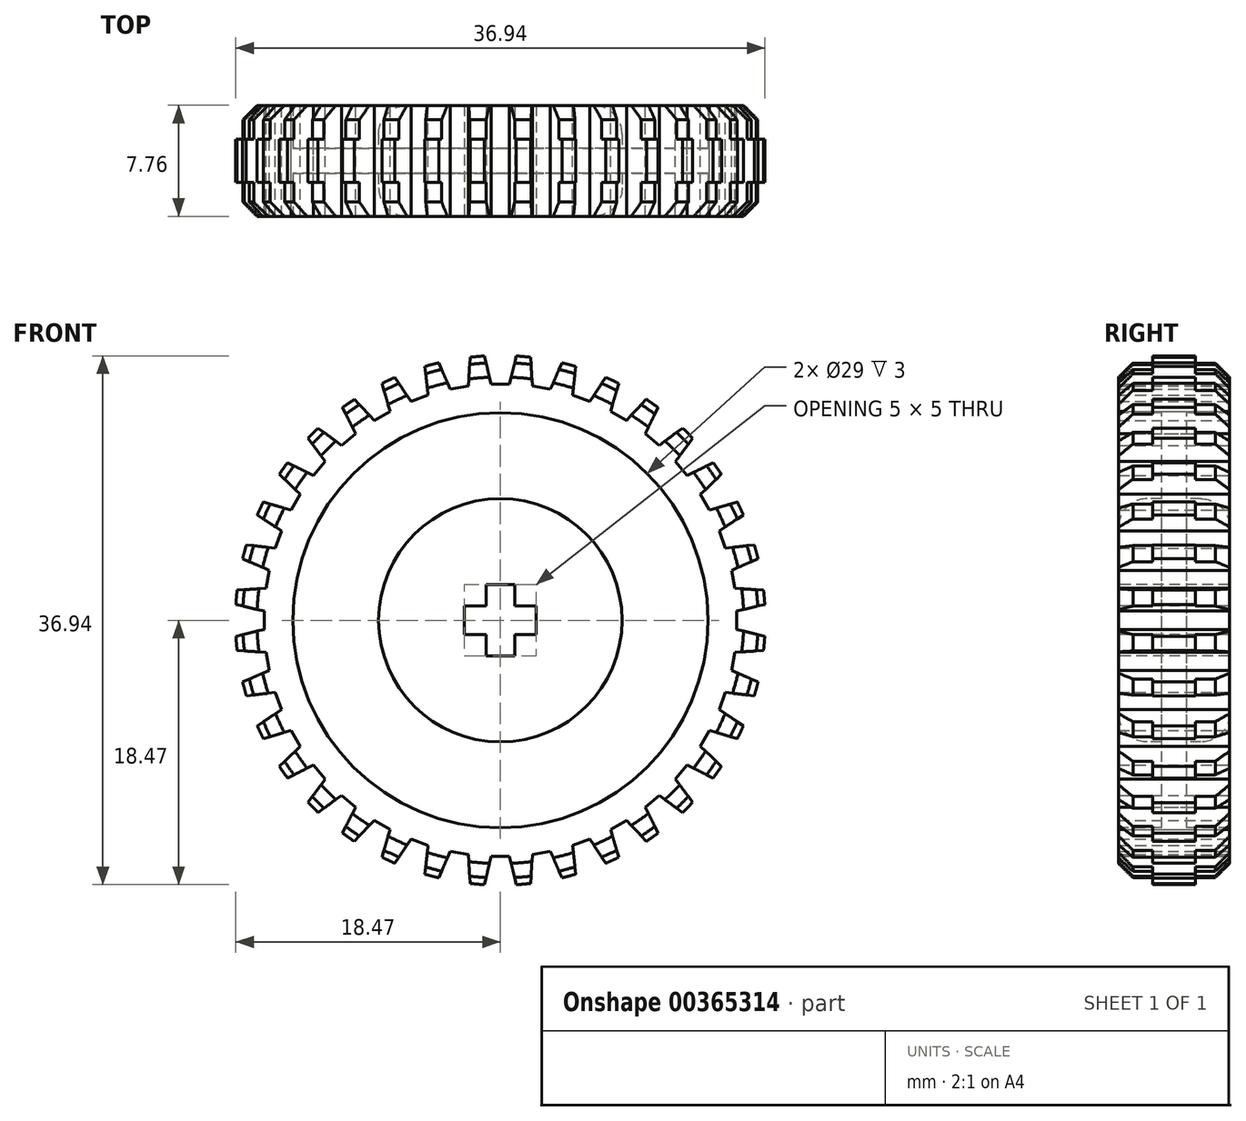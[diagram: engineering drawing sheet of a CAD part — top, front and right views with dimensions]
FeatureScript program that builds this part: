
annotation { "Feature Type Name" : "Feature", "Feature Type Description" : "" }
export const myFeature = defineFeature(function(context is Context, id is Id, definition is map)
    precondition{}
    {
        {
            var Q0;
            Q0=qCreatedBy(makeId("Right.planeOp"),FACE);
            var sketch = newSketch(context, id + "F0", { "sketchPlane" : qUnion([Q0])});
            skLineSegment(sketch, "E0", {"start": v(0, 0) * mm, "end": v(0, 18.5) * mm, "construction": true});
            skLineSegment(sketch, "E1", {"start": v(0, 0) * mm, "end": v(13.72, 0) * mm, "construction": true});
            skLineSegment(sketch, "E2", {"start": v(3.88, 6.5) * mm, "end": v(3.88, 0) * mm});
            skPoint(sketch, "E3.visualSharp", {"position": v(3.88, 18.5) * mm});
            skPoint(sketch, "E4.visualSharp", {"position": v(3.88, 8.5) * mm});
            skArc(sketch, "E4.filletArc", {"start": v(3.88, 6.5) * mm, "mid": v(3.29, 7.91) * mm, "end": v(1.88, 8.5) * mm});
            skArc(sketch, "E5.MirrorCS", {"start": v(-3.88, 6.5) * mm, "mid": v(-3.29, 7.91) * mm, "end": v(-1.88, 8.5) * mm});
            skLineSegment(sketch, "E6.MirrorCS", {"start": v(-3.88, 6.5) * mm, "end": v(-3.88, 0) * mm});
            skLineSegment(sketch, "E7", {"start": v(-3.88, 0) * mm, "end": v(3.88, 0) * mm});
            skLineSegment(sketch, "E8", {"start": v(0, 18.5) * mm, "end": v(1.5, 18.5) * mm});
            skLineSegment(sketch, "E9", {"start": v(3.88, 18) * mm, "end": v(3.88, 14.5) * mm});
            skLineSegment(sketch, "E10", {"start": v(3.88, 14.5) * mm, "end": v(0.87, 14.5) * mm});
            skLineSegment(sketch, "E11", {"start": v(0.87, 14.5) * mm, "end": v(0.87, 8.5) * mm});
            skLineSegment(sketch, "E12", {"start": v(0.87, 8.5) * mm, "end": v(1.88, 8.5) * mm});
            skLineSegment(sketch, "E13.MirrorCS", {"start": v(-3.88, 14.5) * mm, "end": v(-0.87, 14.5) * mm});
            skLineSegment(sketch, "E14.MirrorCS", {"start": v(-0.87, 14.5) * mm, "end": v(-0.87, 8.5) * mm});
            skLineSegment(sketch, "E15.MirrorCS", {"start": v(-0.87, 8.5) * mm, "end": v(-1.88, 8.5) * mm});
            skLineSegment(sketch, "E16", {"start": v(1.5, 18.5) * mm, "end": v(1.5, 18) * mm});
            skLineSegment(sketch, "E17", {"start": v(1.5, 18) * mm, "end": v(3.88, 18) * mm});
            skLineSegment(sketch, "E18", {"start": v(3.88, 18) * mm, "end": v(3.88, 18.5) * mm, "construction": true});
            skLineSegment(sketch, "E19", {"start": v(1.5, 18.5) * mm, "end": v(3.88, 18.5) * mm, "construction": true});
            skLineSegment(sketch, "E20.MirrorCS", {"start": v(0, 18.5) * mm, "end": v(-1.5, 18.5) * mm});
            skLineSegment(sketch, "E21.MirrorCS", {"start": v(-1.5, 18.5) * mm, "end": v(-1.5, 18) * mm});
            skLineSegment(sketch, "E22.MirrorCS", {"start": v(-1.5, 18) * mm, "end": v(-3.88, 18) * mm});
            skLineSegment(sketch, "E23.MirrorCS", {"start": v(-3.88, 18) * mm, "end": v(-3.88, 14.5) * mm});
            skSolve(sketch);
        }
        {
            var Q0;
            Q0=makeQuery(id+"F0.imprint","IMPRINT",FACE,{"disambiguationData":[TD([[makeQuery(id+"F0.imprint","IMPRINT",EDGE,{"derivedFrom":sQuery(id+"F0.wireOp",EDGE,"E2")}),-1.0]])]});
            var Q1;
            Q1=sQuery(id+"F0.wireOp",EDGE,"E1");
            revolve(context, id + "F1", {"entities" : qUnion([Q0]), "axis" : qUnion([Q1]), "revolveType" : RevolveType.FULL});
        }
        {
            var Q0;
            Q0=makeQuery(id+"F1.opRevolve","SWEPT_EDGE",EDGE,{"disambiguationData":[OSD([sQuery(id+"F0.wireOp",EDGE,"E22.MirrorCS"),sQuery(id+"F0.wireOp",EDGE,"E23.MirrorCS")])]});
            var Q1;
            Q1=makeQuery(id+"F1.opRevolve","SWEPT_EDGE",EDGE,{"disambiguationData":[OSD([sQuery(id+"F0.wireOp",EDGE,"E9"),sQuery(id+"F0.wireOp",EDGE,"E17")])]});
            chamfer(context, id + "F2", {"entities" : qUnion([Q0, Q1]), "chamferType" : ChamferType.TWO_OFFSETS, "width1" : 1 * mm, "oppositeDirection" : false, "width2" : 1 * mm, "tangentPropagation" : true});
        }
        {
            var Q0;
            Q0=makeQuery(id+"F1.opRevolve","SWEPT_FACE",FACE,{"disambiguationData":[OSD([sQuery(id+"F0.wireOp",EDGE,"E9")])]});
            var sketch = newSketch(context, id + "F3", { "sketchPlane" : qUnion([Q0])});
            skLineSegment(sketch, "E24", {"start": v(0, -14.33) * mm, "end": v(0, 10.6) * mm, "construction": true});
            skLineSegment(sketch, "E25", {"start": v(-15.88, 1.94) * mm, "end": v(5.64, 1.94) * mm, "construction": true});
            skLineSegment(sketch, "E26", {"start": v(0, 0) * mm, "end": v(-1.61, 18.43) * mm, "construction": true});
            skLineSegment(sketch, "E27", {"start": v(-0.9, 15.97) * mm, "end": v(-0.9, 15.97) * mm});
            skArc(sketch, "E28", {"start": v(-0.9, 15.97) * mm, "mid": v(0, -16) * mm, "end": v(0.9, 15.97) * mm, "construction": true});
            skLineSegment(sketch, "E29", {"start": v(0, 10.6) * mm, "end": v(0, 19.08) * mm, "construction": true});
            skLineSegment(sketch, "E30", {"start": v(0, 16) * mm, "end": v(0, 16.5) * mm});
            skLineSegment(sketch, "E31", {"start": v(0, 16.5) * mm, "end": v(-0.64, 16.5) * mm});
            skLineSegment(sketch, "E32", {"start": v(-0.64, 16.5) * mm, "end": v(-1.44, 16.43) * mm});
            skLineSegment(sketch, "E33", {"start": v(-1.11, 18.47) * mm, "end": v(-0.64, 16.5) * mm});
            skLineSegment(sketch, "E34.MirrorCS", {"start": v(0, 16.5) * mm, "end": v(0.64, 16.5) * mm});
            skLineSegment(sketch, "E35.MirrorCS", {"start": v(1.11, 18.47) * mm, "end": v(0.64, 16.5) * mm});
            skLineSegment(sketch, "E36", {"start": v(-1.61, 18.43) * mm, "end": v(-1.11, 18.47) * mm});
            skLineSegment(sketch, "E37.MirrorCS", {"start": v(1.61, 18.43) * mm, "end": v(1.11, 18.47) * mm});
            skLineSegment(sketch, "E38.1.0", {"start": v(-4.79, 17.87) * mm, "end": v(-4.3, 18) * mm});
            skLineSegment(sketch, "E38.1.1", {"start": v(-4.3, 18) * mm, "end": v(-3.5, 16.14) * mm});
            skLineSegment(sketch, "E38.1.2", {"start": v(-2.87, 16.25) * mm, "end": v(-3.5, 16.14) * mm});
            skLineSegment(sketch, "E38.1.3", {"start": v(-2.87, 16.25) * mm, "end": v(-2.23, 16.36) * mm});
            skLineSegment(sketch, "E38.1.4", {"start": v(-2.11, 18.39) * mm, "end": v(-2.23, 16.36) * mm});
            skLineSegment(sketch, "E38.1.5", {"start": v(-1.61, 18.43) * mm, "end": v(-2.11, 18.39) * mm});
            skLineSegment(sketch, "E38.2.0", {"start": v(-7.82, 16.77) * mm, "end": v(-7.37, 16.98) * mm});
            skLineSegment(sketch, "E38.2.1", {"start": v(-7.37, 16.98) * mm, "end": v(-6.25, 15.29) * mm});
            skLineSegment(sketch, "E38.2.2", {"start": v(-5.64, 15.5) * mm, "end": v(-6.25, 15.29) * mm});
            skLineSegment(sketch, "E38.2.3", {"start": v(-5.64, 15.5) * mm, "end": v(-5.04, 15.72) * mm});
            skLineSegment(sketch, "E38.2.4", {"start": v(-5.27, 17.74) * mm, "end": v(-5.04, 15.72) * mm});
            skLineSegment(sketch, "E38.2.5", {"start": v(-4.79, 17.87) * mm, "end": v(-5.27, 17.74) * mm});
            skLineSegment(sketch, "E39.1.3.0", {"start": v(-10.61, 15.15) * mm, "end": v(-10.2, 15.44) * mm});
            skLineSegment(sketch, "E39.3.3.0", {"start": v(-10.2, 15.44) * mm, "end": v(-8.8, 13.97) * mm});
            skLineSegment(sketch, "E39.6.3.0", {"start": v(-8.25, 14.29) * mm, "end": v(-8.8, 13.97) * mm});
            skLineSegment(sketch, "E39.9.3.0", {"start": v(-8.25, 14.29) * mm, "end": v(-7.7, 14.6) * mm});
            skLineSegment(sketch, "E39.12.3.0", {"start": v(-8.27, 16.56) * mm, "end": v(-7.7, 14.6) * mm});
            skLineSegment(sketch, "E39.15.3.0", {"start": v(-7.82, 16.77) * mm, "end": v(-8.27, 16.56) * mm});
            skLineSegment(sketch, "E39.1.4.0", {"start": v(-13.08, 13.08) * mm, "end": v(-12.73, 13.44) * mm});
            skLineSegment(sketch, "E39.3.4.0", {"start": v(-12.73, 13.44) * mm, "end": v(-11.1, 12.23) * mm});
            skLineSegment(sketch, "E39.6.4.0", {"start": v(-10.6, 12.64) * mm, "end": v(-11.1, 12.23) * mm});
            skLineSegment(sketch, "E39.9.4.0", {"start": v(-10.6, 12.64) * mm, "end": v(-10.12, 13.05) * mm});
            skLineSegment(sketch, "E39.12.4.0", {"start": v(-11.02, 14.87) * mm, "end": v(-10.12, 13.05) * mm});
            skLineSegment(sketch, "E39.15.4.0", {"start": v(-10.61, 15.15) * mm, "end": v(-11.02, 14.87) * mm});
            skLineSegment(sketch, "E39.1.5.0", {"start": v(-15.15, 10.61) * mm, "end": v(-14.87, 11.02) * mm});
            skLineSegment(sketch, "E39.3.5.0", {"start": v(-14.87, 11.02) * mm, "end": v(-13.05, 10.12) * mm});
            skLineSegment(sketch, "E39.6.5.0", {"start": v(-12.64, 10.6) * mm, "end": v(-13.05, 10.12) * mm});
            skLineSegment(sketch, "E39.9.5.0", {"start": v(-12.64, 10.6) * mm, "end": v(-12.23, 11.1) * mm});
            skLineSegment(sketch, "E39.12.5.0", {"start": v(-13.44, 12.73) * mm, "end": v(-12.23, 11.1) * mm});
            skLineSegment(sketch, "E39.15.5.0", {"start": v(-13.08, 13.08) * mm, "end": v(-13.44, 12.73) * mm});
            skLineSegment(sketch, "E39.1.6.0", {"start": v(-16.77, 7.82) * mm, "end": v(-16.56, 8.27) * mm});
            skLineSegment(sketch, "E39.3.6.0", {"start": v(-16.56, 8.27) * mm, "end": v(-14.6, 7.7) * mm});
            skLineSegment(sketch, "E39.6.6.0", {"start": v(-14.29, 8.25) * mm, "end": v(-14.6, 7.7) * mm});
            skLineSegment(sketch, "E39.9.6.0", {"start": v(-14.29, 8.25) * mm, "end": v(-13.97, 8.8) * mm});
            skLineSegment(sketch, "E39.12.6.0", {"start": v(-15.44, 10.2) * mm, "end": v(-13.97, 8.8) * mm});
            skLineSegment(sketch, "E39.15.6.0", {"start": v(-15.15, 10.61) * mm, "end": v(-15.44, 10.2) * mm});
            skLineSegment(sketch, "E39.1.7.0", {"start": v(-17.87, 4.79) * mm, "end": v(-17.74, 5.27) * mm});
            skLineSegment(sketch, "E39.3.7.0", {"start": v(-17.74, 5.27) * mm, "end": v(-15.72, 5.04) * mm});
            skLineSegment(sketch, "E39.6.7.0", {"start": v(-15.5, 5.64) * mm, "end": v(-15.72, 5.04) * mm});
            skLineSegment(sketch, "E39.9.7.0", {"start": v(-15.5, 5.64) * mm, "end": v(-15.29, 6.25) * mm});
            skLineSegment(sketch, "E39.12.7.0", {"start": v(-16.98, 7.37) * mm, "end": v(-15.29, 6.25) * mm});
            skLineSegment(sketch, "E39.15.7.0", {"start": v(-16.77, 7.82) * mm, "end": v(-16.98, 7.37) * mm});
            skLineSegment(sketch, "E39.1.8.0", {"start": v(-18.43, 1.61) * mm, "end": v(-18.39, 2.11) * mm});
            skLineSegment(sketch, "E39.3.8.0", {"start": v(-18.39, 2.11) * mm, "end": v(-16.36, 2.23) * mm});
            skLineSegment(sketch, "E39.6.8.0", {"start": v(-16.25, 2.87) * mm, "end": v(-16.36, 2.23) * mm});
            skLineSegment(sketch, "E39.9.8.0", {"start": v(-16.25, 2.87) * mm, "end": v(-16.14, 3.5) * mm});
            skLineSegment(sketch, "E39.12.8.0", {"start": v(-18, 4.3) * mm, "end": v(-16.14, 3.5) * mm});
            skLineSegment(sketch, "E39.15.8.0", {"start": v(-17.87, 4.79) * mm, "end": v(-18, 4.3) * mm});
            skLineSegment(sketch, "E39.1.9.0", {"start": v(-18.43, -1.61) * mm, "end": v(-18.47, -1.11) * mm});
            skLineSegment(sketch, "E39.3.9.0", {"start": v(-18.47, -1.11) * mm, "end": v(-16.5, -0.64) * mm});
            skLineSegment(sketch, "E39.6.9.0", {"start": v(-16.5, 0) * mm, "end": v(-16.5, -0.64) * mm});
            skLineSegment(sketch, "E39.9.9.0", {"start": v(-16.5, 0) * mm, "end": v(-16.5, 0.64) * mm});
            skLineSegment(sketch, "E39.12.9.0", {"start": v(-18.47, 1.11) * mm, "end": v(-16.5, 0.64) * mm});
            skLineSegment(sketch, "E39.15.9.0", {"start": v(-18.43, 1.61) * mm, "end": v(-18.47, 1.11) * mm});
            skLineSegment(sketch, "E39.1.10.0", {"start": v(-17.87, -4.79) * mm, "end": v(-18, -4.3) * mm});
            skLineSegment(sketch, "E39.3.10.0", {"start": v(-18, -4.3) * mm, "end": v(-16.14, -3.5) * mm});
            skLineSegment(sketch, "E39.6.10.0", {"start": v(-16.25, -2.87) * mm, "end": v(-16.14, -3.5) * mm});
            skLineSegment(sketch, "E39.9.10.0", {"start": v(-16.25, -2.87) * mm, "end": v(-16.36, -2.23) * mm});
            skLineSegment(sketch, "E39.12.10.0", {"start": v(-18.39, -2.11) * mm, "end": v(-16.36, -2.23) * mm});
            skLineSegment(sketch, "E39.15.10.0", {"start": v(-18.43, -1.61) * mm, "end": v(-18.39, -2.11) * mm});
            skLineSegment(sketch, "E39.1.11.0", {"start": v(-16.77, -7.82) * mm, "end": v(-16.98, -7.37) * mm});
            skLineSegment(sketch, "E39.3.11.0", {"start": v(-16.98, -7.37) * mm, "end": v(-15.29, -6.25) * mm});
            skLineSegment(sketch, "E39.6.11.0", {"start": v(-15.5, -5.64) * mm, "end": v(-15.29, -6.25) * mm});
            skLineSegment(sketch, "E39.9.11.0", {"start": v(-15.5, -5.64) * mm, "end": v(-15.72, -5.04) * mm});
            skLineSegment(sketch, "E39.12.11.0", {"start": v(-17.74, -5.27) * mm, "end": v(-15.72, -5.04) * mm});
            skLineSegment(sketch, "E39.15.11.0", {"start": v(-17.87, -4.79) * mm, "end": v(-17.74, -5.27) * mm});
            skLineSegment(sketch, "E39.1.12.0", {"start": v(-15.15, -10.61) * mm, "end": v(-15.44, -10.2) * mm});
            skLineSegment(sketch, "E39.3.12.0", {"start": v(-15.44, -10.2) * mm, "end": v(-13.97, -8.8) * mm});
            skLineSegment(sketch, "E39.6.12.0", {"start": v(-14.29, -8.25) * mm, "end": v(-13.97, -8.8) * mm});
            skLineSegment(sketch, "E39.9.12.0", {"start": v(-14.29, -8.25) * mm, "end": v(-14.6, -7.7) * mm});
            skLineSegment(sketch, "E39.12.12.0", {"start": v(-16.56, -8.27) * mm, "end": v(-14.6, -7.7) * mm});
            skLineSegment(sketch, "E39.15.12.0", {"start": v(-16.77, -7.82) * mm, "end": v(-16.56, -8.27) * mm});
            skLineSegment(sketch, "E39.1.13.0", {"start": v(-13.08, -13.08) * mm, "end": v(-13.44, -12.73) * mm});
            skLineSegment(sketch, "E39.3.13.0", {"start": v(-13.44, -12.73) * mm, "end": v(-12.23, -11.1) * mm});
            skLineSegment(sketch, "E39.6.13.0", {"start": v(-12.64, -10.6) * mm, "end": v(-12.23, -11.1) * mm});
            skLineSegment(sketch, "E39.9.13.0", {"start": v(-12.64, -10.6) * mm, "end": v(-13.05, -10.12) * mm});
            skLineSegment(sketch, "E39.12.13.0", {"start": v(-14.87, -11.02) * mm, "end": v(-13.05, -10.12) * mm});
            skLineSegment(sketch, "E39.15.13.0", {"start": v(-15.15, -10.61) * mm, "end": v(-14.87, -11.02) * mm});
            skLineSegment(sketch, "E39.1.14.0", {"start": v(-10.61, -15.15) * mm, "end": v(-11.02, -14.87) * mm});
            skLineSegment(sketch, "E39.3.14.0", {"start": v(-11.02, -14.87) * mm, "end": v(-10.12, -13.05) * mm});
            skLineSegment(sketch, "E39.6.14.0", {"start": v(-10.6, -12.64) * mm, "end": v(-10.12, -13.05) * mm});
            skLineSegment(sketch, "E39.9.14.0", {"start": v(-10.6, -12.64) * mm, "end": v(-11.1, -12.23) * mm});
            skLineSegment(sketch, "E39.12.14.0", {"start": v(-12.73, -13.44) * mm, "end": v(-11.1, -12.23) * mm});
            skLineSegment(sketch, "E39.15.14.0", {"start": v(-13.08, -13.08) * mm, "end": v(-12.73, -13.44) * mm});
            skLineSegment(sketch, "E39.1.15.0", {"start": v(-7.82, -16.77) * mm, "end": v(-8.27, -16.56) * mm});
            skLineSegment(sketch, "E39.3.15.0", {"start": v(-8.27, -16.56) * mm, "end": v(-7.7, -14.6) * mm});
            skLineSegment(sketch, "E39.6.15.0", {"start": v(-8.25, -14.29) * mm, "end": v(-7.7, -14.6) * mm});
            skLineSegment(sketch, "E39.9.15.0", {"start": v(-8.25, -14.29) * mm, "end": v(-8.8, -13.97) * mm});
            skLineSegment(sketch, "E39.12.15.0", {"start": v(-10.2, -15.44) * mm, "end": v(-8.8, -13.97) * mm});
            skLineSegment(sketch, "E39.15.15.0", {"start": v(-10.61, -15.15) * mm, "end": v(-10.2, -15.44) * mm});
            skLineSegment(sketch, "E39.1.16.0", {"start": v(-4.79, -17.87) * mm, "end": v(-5.27, -17.74) * mm});
            skLineSegment(sketch, "E39.3.16.0", {"start": v(-5.27, -17.74) * mm, "end": v(-5.04, -15.72) * mm});
            skLineSegment(sketch, "E39.6.16.0", {"start": v(-5.64, -15.5) * mm, "end": v(-5.04, -15.72) * mm});
            skLineSegment(sketch, "E39.9.16.0", {"start": v(-5.64, -15.5) * mm, "end": v(-6.25, -15.29) * mm});
            skLineSegment(sketch, "E39.12.16.0", {"start": v(-7.37, -16.98) * mm, "end": v(-6.25, -15.29) * mm});
            skLineSegment(sketch, "E39.15.16.0", {"start": v(-7.82, -16.77) * mm, "end": v(-7.37, -16.98) * mm});
            skLineSegment(sketch, "E39.1.17.0", {"start": v(-1.61, -18.43) * mm, "end": v(-2.11, -18.39) * mm});
            skLineSegment(sketch, "E39.3.17.0", {"start": v(-2.11, -18.39) * mm, "end": v(-2.23, -16.36) * mm});
            skLineSegment(sketch, "E39.6.17.0", {"start": v(-2.87, -16.25) * mm, "end": v(-2.23, -16.36) * mm});
            skLineSegment(sketch, "E39.9.17.0", {"start": v(-2.87, -16.25) * mm, "end": v(-3.5, -16.14) * mm});
            skLineSegment(sketch, "E39.12.17.0", {"start": v(-4.3, -18) * mm, "end": v(-3.5, -16.14) * mm});
            skLineSegment(sketch, "E39.15.17.0", {"start": v(-4.79, -17.87) * mm, "end": v(-4.3, -18) * mm});
            skLineSegment(sketch, "E39.1.18.0", {"start": v(1.61, -18.43) * mm, "end": v(1.11, -18.47) * mm});
            skLineSegment(sketch, "E39.3.18.0", {"start": v(1.11, -18.47) * mm, "end": v(0.64, -16.5) * mm});
            skLineSegment(sketch, "E39.6.18.0", {"start": v(0, -16.5) * mm, "end": v(0.64, -16.5) * mm});
            skLineSegment(sketch, "E39.9.18.0", {"start": v(0, -16.5) * mm, "end": v(-0.64, -16.5) * mm});
            skLineSegment(sketch, "E39.12.18.0", {"start": v(-1.11, -18.47) * mm, "end": v(-0.64, -16.5) * mm});
            skLineSegment(sketch, "E39.15.18.0", {"start": v(-1.61, -18.43) * mm, "end": v(-1.11, -18.47) * mm});
            skLineSegment(sketch, "E39.1.19.0", {"start": v(4.79, -17.87) * mm, "end": v(4.3, -18) * mm});
            skLineSegment(sketch, "E39.3.19.0", {"start": v(4.3, -18) * mm, "end": v(3.5, -16.14) * mm});
            skLineSegment(sketch, "E39.6.19.0", {"start": v(2.87, -16.25) * mm, "end": v(3.5, -16.14) * mm});
            skLineSegment(sketch, "E39.9.19.0", {"start": v(2.87, -16.25) * mm, "end": v(2.23, -16.36) * mm});
            skLineSegment(sketch, "E39.12.19.0", {"start": v(2.11, -18.39) * mm, "end": v(2.23, -16.36) * mm});
            skLineSegment(sketch, "E39.15.19.0", {"start": v(1.61, -18.43) * mm, "end": v(2.11, -18.39) * mm});
            skLineSegment(sketch, "E39.1.20.0", {"start": v(7.82, -16.77) * mm, "end": v(7.37, -16.98) * mm});
            skLineSegment(sketch, "E39.3.20.0", {"start": v(7.37, -16.98) * mm, "end": v(6.25, -15.29) * mm});
            skLineSegment(sketch, "E39.6.20.0", {"start": v(5.64, -15.5) * mm, "end": v(6.25, -15.29) * mm});
            skLineSegment(sketch, "E39.9.20.0", {"start": v(5.64, -15.5) * mm, "end": v(5.04, -15.72) * mm});
            skLineSegment(sketch, "E39.12.20.0", {"start": v(5.27, -17.74) * mm, "end": v(5.04, -15.72) * mm});
            skLineSegment(sketch, "E39.15.20.0", {"start": v(4.79, -17.87) * mm, "end": v(5.27, -17.74) * mm});
            skLineSegment(sketch, "E39.1.21.0", {"start": v(10.61, -15.15) * mm, "end": v(10.2, -15.44) * mm});
            skLineSegment(sketch, "E39.3.21.0", {"start": v(10.2, -15.44) * mm, "end": v(8.8, -13.97) * mm});
            skLineSegment(sketch, "E39.6.21.0", {"start": v(8.25, -14.29) * mm, "end": v(8.8, -13.97) * mm});
            skLineSegment(sketch, "E39.9.21.0", {"start": v(8.25, -14.29) * mm, "end": v(7.7, -14.6) * mm});
            skLineSegment(sketch, "E39.12.21.0", {"start": v(8.27, -16.56) * mm, "end": v(7.7, -14.6) * mm});
            skLineSegment(sketch, "E39.15.21.0", {"start": v(7.82, -16.77) * mm, "end": v(8.27, -16.56) * mm});
            skLineSegment(sketch, "E39.1.22.0", {"start": v(13.08, -13.08) * mm, "end": v(12.73, -13.44) * mm});
            skLineSegment(sketch, "E39.3.22.0", {"start": v(12.73, -13.44) * mm, "end": v(11.1, -12.23) * mm});
            skLineSegment(sketch, "E39.6.22.0", {"start": v(10.6, -12.64) * mm, "end": v(11.1, -12.23) * mm});
            skLineSegment(sketch, "E39.9.22.0", {"start": v(10.6, -12.64) * mm, "end": v(10.12, -13.05) * mm});
            skLineSegment(sketch, "E39.12.22.0", {"start": v(11.02, -14.87) * mm, "end": v(10.12, -13.05) * mm});
            skLineSegment(sketch, "E39.15.22.0", {"start": v(10.61, -15.15) * mm, "end": v(11.02, -14.87) * mm});
            skLineSegment(sketch, "E39.1.23.0", {"start": v(15.15, -10.61) * mm, "end": v(14.87, -11.02) * mm});
            skLineSegment(sketch, "E39.3.23.0", {"start": v(14.87, -11.02) * mm, "end": v(13.05, -10.12) * mm});
            skLineSegment(sketch, "E39.6.23.0", {"start": v(12.64, -10.6) * mm, "end": v(13.05, -10.12) * mm});
            skLineSegment(sketch, "E39.9.23.0", {"start": v(12.64, -10.6) * mm, "end": v(12.23, -11.1) * mm});
            skLineSegment(sketch, "E39.12.23.0", {"start": v(13.44, -12.73) * mm, "end": v(12.23, -11.1) * mm});
            skLineSegment(sketch, "E39.15.23.0", {"start": v(13.08, -13.08) * mm, "end": v(13.44, -12.73) * mm});
            skLineSegment(sketch, "E39.1.24.0", {"start": v(16.77, -7.82) * mm, "end": v(16.56, -8.27) * mm});
            skLineSegment(sketch, "E39.3.24.0", {"start": v(16.56, -8.27) * mm, "end": v(14.6, -7.7) * mm});
            skLineSegment(sketch, "E39.6.24.0", {"start": v(14.29, -8.25) * mm, "end": v(14.6, -7.7) * mm});
            skLineSegment(sketch, "E39.9.24.0", {"start": v(14.29, -8.25) * mm, "end": v(13.97, -8.8) * mm});
            skLineSegment(sketch, "E39.12.24.0", {"start": v(15.44, -10.2) * mm, "end": v(13.97, -8.8) * mm});
            skLineSegment(sketch, "E39.15.24.0", {"start": v(15.15, -10.61) * mm, "end": v(15.44, -10.2) * mm});
            skLineSegment(sketch, "E39.1.25.0", {"start": v(17.87, -4.79) * mm, "end": v(17.74, -5.27) * mm});
            skLineSegment(sketch, "E39.3.25.0", {"start": v(17.74, -5.27) * mm, "end": v(15.72, -5.04) * mm});
            skLineSegment(sketch, "E39.6.25.0", {"start": v(15.5, -5.64) * mm, "end": v(15.72, -5.04) * mm});
            skLineSegment(sketch, "E39.9.25.0", {"start": v(15.5, -5.64) * mm, "end": v(15.29, -6.25) * mm});
            skLineSegment(sketch, "E39.12.25.0", {"start": v(16.98, -7.37) * mm, "end": v(15.29, -6.25) * mm});
            skLineSegment(sketch, "E39.15.25.0", {"start": v(16.77, -7.82) * mm, "end": v(16.98, -7.37) * mm});
            skLineSegment(sketch, "E39.1.26.0", {"start": v(18.43, -1.61) * mm, "end": v(18.39, -2.11) * mm});
            skLineSegment(sketch, "E39.3.26.0", {"start": v(18.39, -2.11) * mm, "end": v(16.36, -2.23) * mm});
            skLineSegment(sketch, "E39.6.26.0", {"start": v(16.25, -2.87) * mm, "end": v(16.36, -2.23) * mm});
            skLineSegment(sketch, "E39.9.26.0", {"start": v(16.25, -2.87) * mm, "end": v(16.14, -3.5) * mm});
            skLineSegment(sketch, "E39.12.26.0", {"start": v(18, -4.3) * mm, "end": v(16.14, -3.5) * mm});
            skLineSegment(sketch, "E39.15.26.0", {"start": v(17.87, -4.79) * mm, "end": v(18, -4.3) * mm});
            skLineSegment(sketch, "E39.1.27.0", {"start": v(18.43, 1.61) * mm, "end": v(18.47, 1.11) * mm});
            skLineSegment(sketch, "E39.3.27.0", {"start": v(18.47, 1.11) * mm, "end": v(16.5, 0.64) * mm});
            skLineSegment(sketch, "E39.6.27.0", {"start": v(16.5, 0) * mm, "end": v(16.5, 0.64) * mm});
            skLineSegment(sketch, "E39.9.27.0", {"start": v(16.5, 0) * mm, "end": v(16.5, -0.64) * mm});
            skLineSegment(sketch, "E39.12.27.0", {"start": v(18.47, -1.11) * mm, "end": v(16.5, -0.64) * mm});
            skLineSegment(sketch, "E39.15.27.0", {"start": v(18.43, -1.61) * mm, "end": v(18.47, -1.11) * mm});
            skLineSegment(sketch, "E39.1.28.0", {"start": v(17.87, 4.79) * mm, "end": v(18, 4.3) * mm});
            skLineSegment(sketch, "E39.3.28.0", {"start": v(18, 4.3) * mm, "end": v(16.14, 3.5) * mm});
            skLineSegment(sketch, "E39.6.28.0", {"start": v(16.25, 2.87) * mm, "end": v(16.14, 3.5) * mm});
            skLineSegment(sketch, "E39.9.28.0", {"start": v(16.25, 2.87) * mm, "end": v(16.36, 2.23) * mm});
            skLineSegment(sketch, "E39.12.28.0", {"start": v(18.39, 2.11) * mm, "end": v(16.36, 2.23) * mm});
            skLineSegment(sketch, "E39.15.28.0", {"start": v(18.43, 1.61) * mm, "end": v(18.39, 2.11) * mm});
            skLineSegment(sketch, "E39.1.29.0", {"start": v(16.77, 7.82) * mm, "end": v(16.98, 7.37) * mm});
            skLineSegment(sketch, "E39.3.29.0", {"start": v(16.98, 7.37) * mm, "end": v(15.29, 6.25) * mm});
            skLineSegment(sketch, "E39.6.29.0", {"start": v(15.5, 5.64) * mm, "end": v(15.29, 6.25) * mm});
            skLineSegment(sketch, "E39.9.29.0", {"start": v(15.5, 5.64) * mm, "end": v(15.72, 5.04) * mm});
            skLineSegment(sketch, "E39.12.29.0", {"start": v(17.74, 5.27) * mm, "end": v(15.72, 5.04) * mm});
            skLineSegment(sketch, "E39.15.29.0", {"start": v(17.87, 4.79) * mm, "end": v(17.74, 5.27) * mm});
            skLineSegment(sketch, "E39.1.30.0", {"start": v(15.15, 10.61) * mm, "end": v(15.44, 10.2) * mm});
            skLineSegment(sketch, "E39.3.30.0", {"start": v(15.44, 10.2) * mm, "end": v(13.97, 8.8) * mm});
            skLineSegment(sketch, "E39.6.30.0", {"start": v(14.29, 8.25) * mm, "end": v(13.97, 8.8) * mm});
            skLineSegment(sketch, "E39.9.30.0", {"start": v(14.29, 8.25) * mm, "end": v(14.6, 7.7) * mm});
            skLineSegment(sketch, "E39.12.30.0", {"start": v(16.56, 8.27) * mm, "end": v(14.6, 7.7) * mm});
            skLineSegment(sketch, "E39.15.30.0", {"start": v(16.77, 7.82) * mm, "end": v(16.56, 8.27) * mm});
            skLineSegment(sketch, "E39.1.31.0", {"start": v(13.08, 13.08) * mm, "end": v(13.44, 12.73) * mm});
            skLineSegment(sketch, "E39.3.31.0", {"start": v(13.44, 12.73) * mm, "end": v(12.23, 11.1) * mm});
            skLineSegment(sketch, "E39.6.31.0", {"start": v(12.64, 10.6) * mm, "end": v(12.23, 11.1) * mm});
            skLineSegment(sketch, "E39.9.31.0", {"start": v(12.64, 10.6) * mm, "end": v(13.05, 10.12) * mm});
            skLineSegment(sketch, "E39.12.31.0", {"start": v(14.87, 11.02) * mm, "end": v(13.05, 10.12) * mm});
            skLineSegment(sketch, "E39.15.31.0", {"start": v(15.15, 10.61) * mm, "end": v(14.87, 11.02) * mm});
            skLineSegment(sketch, "E39.1.32.0", {"start": v(10.61, 15.15) * mm, "end": v(11.02, 14.87) * mm});
            skLineSegment(sketch, "E39.3.32.0", {"start": v(11.02, 14.87) * mm, "end": v(10.12, 13.05) * mm});
            skLineSegment(sketch, "E39.6.32.0", {"start": v(10.6, 12.64) * mm, "end": v(10.12, 13.05) * mm});
            skLineSegment(sketch, "E39.9.32.0", {"start": v(10.6, 12.64) * mm, "end": v(11.1, 12.23) * mm});
            skLineSegment(sketch, "E39.12.32.0", {"start": v(12.73, 13.44) * mm, "end": v(11.1, 12.23) * mm});
            skLineSegment(sketch, "E39.15.32.0", {"start": v(13.08, 13.08) * mm, "end": v(12.73, 13.44) * mm});
            skLineSegment(sketch, "E39.1.33.0", {"start": v(7.82, 16.77) * mm, "end": v(8.27, 16.56) * mm});
            skLineSegment(sketch, "E39.3.33.0", {"start": v(8.27, 16.56) * mm, "end": v(7.7, 14.6) * mm});
            skLineSegment(sketch, "E39.6.33.0", {"start": v(8.25, 14.29) * mm, "end": v(7.7, 14.6) * mm});
            skLineSegment(sketch, "E39.9.33.0", {"start": v(8.25, 14.29) * mm, "end": v(8.8, 13.97) * mm});
            skLineSegment(sketch, "E39.12.33.0", {"start": v(10.2, 15.44) * mm, "end": v(8.8, 13.97) * mm});
            skLineSegment(sketch, "E39.15.33.0", {"start": v(10.61, 15.15) * mm, "end": v(10.2, 15.44) * mm});
            skLineSegment(sketch, "E39.1.34.0", {"start": v(4.79, 17.87) * mm, "end": v(5.27, 17.74) * mm});
            skLineSegment(sketch, "E39.3.34.0", {"start": v(5.27, 17.74) * mm, "end": v(5.04, 15.72) * mm});
            skLineSegment(sketch, "E39.6.34.0", {"start": v(5.64, 15.5) * mm, "end": v(5.04, 15.72) * mm});
            skLineSegment(sketch, "E39.9.34.0", {"start": v(5.64, 15.5) * mm, "end": v(6.25, 15.29) * mm});
            skLineSegment(sketch, "E39.12.34.0", {"start": v(7.37, 16.98) * mm, "end": v(6.25, 15.29) * mm});
            skLineSegment(sketch, "E39.15.34.0", {"start": v(7.82, 16.77) * mm, "end": v(7.37, 16.98) * mm});
            skLineSegment(sketch, "E39.1.35.0", {"start": v(1.61, 18.43) * mm, "end": v(2.11, 18.39) * mm});
            skLineSegment(sketch, "E39.3.35.0", {"start": v(2.11, 18.39) * mm, "end": v(2.23, 16.36) * mm});
            skLineSegment(sketch, "E39.6.35.0", {"start": v(2.87, 16.25) * mm, "end": v(2.23, 16.36) * mm});
            skLineSegment(sketch, "E39.9.35.0", {"start": v(2.87, 16.25) * mm, "end": v(3.5, 16.14) * mm});
            skLineSegment(sketch, "E39.12.35.0", {"start": v(4.3, 18) * mm, "end": v(3.5, 16.14) * mm});
            skLineSegment(sketch, "E39.15.35.0", {"start": v(4.79, 17.87) * mm, "end": v(4.3, 18) * mm});
            skSolve(sketch);
        }
        {
            var Q0;
            Q0=makeQuery(id+"F3.imprint","IMPRINT",FACE,{"disambiguationData":[TD([[makeQuery(id+"F3.imprint","IMPRINT",EDGE,{"derivedFrom":makeQuery(id+"F1.opRevolve","SWEPT_EDGE",EDGE,{"disambiguationData":[OSD([sQuery(id+"F0.wireOp",EDGE,"E9"),sQuery(id+"F0.wireOp",EDGE,"E10")])]})}),-1.0]])]});
            var Q1;
            {var subQ1=sQuery(id+"F3.wireOp",EDGE,"2c81646e-4cb3-4f6a-b688-8c6a1ed544cc.6.1");Q1=makeQuery(id+"F3.imprint","IMPRINT",FACE,{"disambiguationData":[TD([[makeQuery(id+"F3.imprint","IMPRINT",EDGE,{"derivedFrom":subQ1}),-1.0]])]});}
            var Q2;
            {var subQ14=sQuery(id+"F3.wireOp",EDGE,"989202d4-2dea-47d2-9641-2749aa3cc128");Q2=makeQuery(id+"F3.imprint","IMPRINT",FACE,{"disambiguationData":[TD([[makeQuery(id+"F3.imprint","IMPRINT",EDGE,{"derivedFrom":subQ14}),1.0]])]});}
            var Q3;
            {var subQ1=sQuery(id+"F3.wireOp",EDGE,"2c81646e-4cb3-4f6a-b688-8c6a1ed544cc.5.1");Q3=makeQuery(id+"F3.imprint","IMPRINT",FACE,{"disambiguationData":[TD([[makeQuery(id+"F3.imprint","IMPRINT",EDGE,{"derivedFrom":subQ1}),-1.0]])]});}
            var Q4;
            {var subQ1=sQuery(id+"F3.wireOp",EDGE,"2c81646e-4cb3-4f6a-b688-8c6a1ed544cc.4.1");Q4=makeQuery(id+"F3.imprint","IMPRINT",FACE,{"disambiguationData":[TD([[makeQuery(id+"F3.imprint","IMPRINT",EDGE,{"derivedFrom":subQ1}),-1.0]])]});}
            var Q5;
            {var subQ1=sQuery(id+"F3.wireOp",EDGE,"2c81646e-4cb3-4f6a-b688-8c6a1ed544cc.3.1");Q5=makeQuery(id+"F3.imprint","IMPRINT",FACE,{"disambiguationData":[TD([[makeQuery(id+"F3.imprint","IMPRINT",EDGE,{"derivedFrom":subQ1}),-1.0]])]});}
            var Q6;
            {var subQ1=sQuery(id+"F3.wireOp",EDGE,"2c81646e-4cb3-4f6a-b688-8c6a1ed544cc.2.1");Q6=makeQuery(id+"F3.imprint","IMPRINT",FACE,{"disambiguationData":[TD([[makeQuery(id+"F3.imprint","IMPRINT",EDGE,{"derivedFrom":subQ1}),-1.0]])]});}
            var Q7;
            {var subQ1=sQuery(id+"F3.wireOp",EDGE,"2c81646e-4cb3-4f6a-b688-8c6a1ed544cc.1.1");Q7=makeQuery(id+"F3.imprint","IMPRINT",FACE,{"disambiguationData":[TD([[makeQuery(id+"F3.imprint","IMPRINT",EDGE,{"derivedFrom":subQ1}),-1.0]])]});}
            var Q8;
            {var subQ4=sQuery(id+"F3.wireOp",EDGE,"18cba4a9-fe1b-41df-914d-63172cd125b3");Q8=makeQuery(id+"F3.imprint","IMPRINT",FACE,{"disambiguationData":[TD([[makeQuery(id+"F3.imprint","IMPRINT",EDGE,{"derivedFrom":subQ4}),-1.0]])]});}
            var Q9;
            {var subQ1=sQuery(id+"F3.wireOp",EDGE,"f64b6125-3031-4aec-bc3c-2336ab89e1f2.MirrorCS");Q9=makeQuery(id+"F3.imprint","IMPRINT",FACE,{"disambiguationData":[TD([[makeQuery(id+"F3.imprint","IMPRINT",EDGE,{"derivedFrom":subQ1}),1.0]])]});}
            var Q10;
            {var subQ1=sQuery(id+"F3.wireOp",EDGE,"2c81646e-4cb3-4f6a-b688-8c6a1ed544cc.34.1");Q10=makeQuery(id+"F3.imprint","IMPRINT",FACE,{"disambiguationData":[TD([[makeQuery(id+"F3.imprint","IMPRINT",EDGE,{"derivedFrom":subQ1}),-1.0]])]});}
            var Q11;
            {var subQ1=sQuery(id+"F3.wireOp",EDGE,"2c81646e-4cb3-4f6a-b688-8c6a1ed544cc.33.1");Q11=makeQuery(id+"F3.imprint","IMPRINT",FACE,{"disambiguationData":[TD([[makeQuery(id+"F3.imprint","IMPRINT",EDGE,{"derivedFrom":subQ1}),-1.0]])]});}
            var Q12;
            {var subQ1=sQuery(id+"F3.wireOp",EDGE,"2c81646e-4cb3-4f6a-b688-8c6a1ed544cc.32.1");Q12=makeQuery(id+"F3.imprint","IMPRINT",FACE,{"disambiguationData":[TD([[makeQuery(id+"F3.imprint","IMPRINT",EDGE,{"derivedFrom":subQ1}),-1.0]])]});}
            var Q13;
            {var subQ1=sQuery(id+"F3.wireOp",EDGE,"2c81646e-4cb3-4f6a-b688-8c6a1ed544cc.31.1");Q13=makeQuery(id+"F3.imprint","IMPRINT",FACE,{"disambiguationData":[TD([[makeQuery(id+"F3.imprint","IMPRINT",EDGE,{"derivedFrom":subQ1}),-1.0]])]});}
            var Q14;
            {var subQ1=sQuery(id+"F3.wireOp",EDGE,"2c81646e-4cb3-4f6a-b688-8c6a1ed544cc.30.1");Q14=makeQuery(id+"F3.imprint","IMPRINT",FACE,{"disambiguationData":[TD([[makeQuery(id+"F3.imprint","IMPRINT",EDGE,{"derivedFrom":subQ1}),-1.0]])]});}
            var Q15;
            {var subQ1=sQuery(id+"F3.wireOp",EDGE,"2c81646e-4cb3-4f6a-b688-8c6a1ed544cc.29.1");Q15=makeQuery(id+"F3.imprint","IMPRINT",FACE,{"disambiguationData":[TD([[makeQuery(id+"F3.imprint","IMPRINT",EDGE,{"derivedFrom":subQ1}),-1.0]])]});}
            var Q16;
            {var subQ1=sQuery(id+"F3.wireOp",EDGE,"2c81646e-4cb3-4f6a-b688-8c6a1ed544cc.28.1");Q16=makeQuery(id+"F3.imprint","IMPRINT",FACE,{"disambiguationData":[TD([[makeQuery(id+"F3.imprint","IMPRINT",EDGE,{"derivedFrom":subQ1}),-1.0]])]});}
            var Q17;
            {var subQ1=sQuery(id+"F3.wireOp",EDGE,"2c81646e-4cb3-4f6a-b688-8c6a1ed544cc.27.1");Q17=makeQuery(id+"F3.imprint","IMPRINT",FACE,{"disambiguationData":[TD([[makeQuery(id+"F3.imprint","IMPRINT",EDGE,{"derivedFrom":subQ1}),-1.0]])]});}
            var Q18;
            {var subQ1=sQuery(id+"F3.wireOp",EDGE,"2c81646e-4cb3-4f6a-b688-8c6a1ed544cc.26.1");Q18=makeQuery(id+"F3.imprint","IMPRINT",FACE,{"disambiguationData":[TD([[makeQuery(id+"F3.imprint","IMPRINT",EDGE,{"derivedFrom":subQ1}),-1.0]])]});}
            var Q19;
            {var subQ1=sQuery(id+"F3.wireOp",EDGE,"2c81646e-4cb3-4f6a-b688-8c6a1ed544cc.25.1");Q19=makeQuery(id+"F3.imprint","IMPRINT",FACE,{"disambiguationData":[TD([[makeQuery(id+"F3.imprint","IMPRINT",EDGE,{"derivedFrom":subQ1}),-1.0]])]});}
            var Q20;
            {var subQ1=sQuery(id+"F3.wireOp",EDGE,"2c81646e-4cb3-4f6a-b688-8c6a1ed544cc.24.1");Q20=makeQuery(id+"F3.imprint","IMPRINT",FACE,{"disambiguationData":[TD([[makeQuery(id+"F3.imprint","IMPRINT",EDGE,{"derivedFrom":subQ1}),-1.0]])]});}
            var Q21;
            {var subQ1=sQuery(id+"F3.wireOp",EDGE,"2c81646e-4cb3-4f6a-b688-8c6a1ed544cc.23.1");Q21=makeQuery(id+"F3.imprint","IMPRINT",FACE,{"disambiguationData":[TD([[makeQuery(id+"F3.imprint","IMPRINT",EDGE,{"derivedFrom":subQ1}),-1.0]])]});}
            var Q22;
            {var subQ1=sQuery(id+"F3.wireOp",EDGE,"2c81646e-4cb3-4f6a-b688-8c6a1ed544cc.22.1");Q22=makeQuery(id+"F3.imprint","IMPRINT",FACE,{"disambiguationData":[TD([[makeQuery(id+"F3.imprint","IMPRINT",EDGE,{"derivedFrom":subQ1}),-1.0]])]});}
            var Q23;
            {var subQ1=sQuery(id+"F3.wireOp",EDGE,"2c81646e-4cb3-4f6a-b688-8c6a1ed544cc.21.1");Q23=makeQuery(id+"F3.imprint","IMPRINT",FACE,{"disambiguationData":[TD([[makeQuery(id+"F3.imprint","IMPRINT",EDGE,{"derivedFrom":subQ1}),-1.0]])]});}
            var Q24;
            {var subQ1=sQuery(id+"F3.wireOp",EDGE,"2c81646e-4cb3-4f6a-b688-8c6a1ed544cc.20.1");Q24=makeQuery(id+"F3.imprint","IMPRINT",FACE,{"disambiguationData":[TD([[makeQuery(id+"F3.imprint","IMPRINT",EDGE,{"derivedFrom":subQ1}),-1.0]])]});}
            var Q25;
            {var subQ1=sQuery(id+"F3.wireOp",EDGE,"2c81646e-4cb3-4f6a-b688-8c6a1ed544cc.19.1");Q25=makeQuery(id+"F3.imprint","IMPRINT",FACE,{"disambiguationData":[TD([[makeQuery(id+"F3.imprint","IMPRINT",EDGE,{"derivedFrom":subQ1}),-1.0]])]});}
            var Q26;
            {var subQ1=sQuery(id+"F3.wireOp",EDGE,"2c81646e-4cb3-4f6a-b688-8c6a1ed544cc.18.1");Q26=makeQuery(id+"F3.imprint","IMPRINT",FACE,{"disambiguationData":[TD([[makeQuery(id+"F3.imprint","IMPRINT",EDGE,{"derivedFrom":subQ1}),-1.0]])]});}
            var Q27;
            {var subQ1=sQuery(id+"F3.wireOp",EDGE,"2c81646e-4cb3-4f6a-b688-8c6a1ed544cc.17.1");Q27=makeQuery(id+"F3.imprint","IMPRINT",FACE,{"disambiguationData":[TD([[makeQuery(id+"F3.imprint","IMPRINT",EDGE,{"derivedFrom":subQ1}),-1.0]])]});}
            var Q28;
            {var subQ1=sQuery(id+"F3.wireOp",EDGE,"2c81646e-4cb3-4f6a-b688-8c6a1ed544cc.16.1");Q28=makeQuery(id+"F3.imprint","IMPRINT",FACE,{"disambiguationData":[TD([[makeQuery(id+"F3.imprint","IMPRINT",EDGE,{"derivedFrom":subQ1}),-1.0]])]});}
            var Q29;
            {var subQ1=sQuery(id+"F3.wireOp",EDGE,"2c81646e-4cb3-4f6a-b688-8c6a1ed544cc.15.1");Q29=makeQuery(id+"F3.imprint","IMPRINT",FACE,{"disambiguationData":[TD([[makeQuery(id+"F3.imprint","IMPRINT",EDGE,{"derivedFrom":subQ1}),-1.0]])]});}
            var Q30;
            {var subQ1=sQuery(id+"F3.wireOp",EDGE,"2c81646e-4cb3-4f6a-b688-8c6a1ed544cc.14.1");Q30=makeQuery(id+"F3.imprint","IMPRINT",FACE,{"disambiguationData":[TD([[makeQuery(id+"F3.imprint","IMPRINT",EDGE,{"derivedFrom":subQ1}),-1.0]])]});}
            var Q31;
            {var subQ1=sQuery(id+"F3.wireOp",EDGE,"2c81646e-4cb3-4f6a-b688-8c6a1ed544cc.13.1");Q31=makeQuery(id+"F3.imprint","IMPRINT",FACE,{"disambiguationData":[TD([[makeQuery(id+"F3.imprint","IMPRINT",EDGE,{"derivedFrom":subQ1}),-1.0]])]});}
            var Q32;
            {var subQ1=sQuery(id+"F3.wireOp",EDGE,"2c81646e-4cb3-4f6a-b688-8c6a1ed544cc.12.1");Q32=makeQuery(id+"F3.imprint","IMPRINT",FACE,{"disambiguationData":[TD([[makeQuery(id+"F3.imprint","IMPRINT",EDGE,{"derivedFrom":subQ1}),-1.0]])]});}
            var Q33;
            {var subQ1=sQuery(id+"F3.wireOp",EDGE,"2c81646e-4cb3-4f6a-b688-8c6a1ed544cc.11.1");Q33=makeQuery(id+"F3.imprint","IMPRINT",FACE,{"disambiguationData":[TD([[makeQuery(id+"F3.imprint","IMPRINT",EDGE,{"derivedFrom":subQ1}),-1.0]])]});}
            var Q34;
            {var subQ1=sQuery(id+"F3.wireOp",EDGE,"2c81646e-4cb3-4f6a-b688-8c6a1ed544cc.10.1");Q34=makeQuery(id+"F3.imprint","IMPRINT",FACE,{"disambiguationData":[TD([[makeQuery(id+"F3.imprint","IMPRINT",EDGE,{"derivedFrom":subQ1}),-1.0]])]});}
            var Q35;
            {var subQ1=sQuery(id+"F3.wireOp",EDGE,"2c81646e-4cb3-4f6a-b688-8c6a1ed544cc.9.1");Q35=makeQuery(id+"F3.imprint","IMPRINT",FACE,{"disambiguationData":[TD([[makeQuery(id+"F3.imprint","IMPRINT",EDGE,{"derivedFrom":subQ1}),-1.0]])]});}
            var Q36;
            {var subQ1=sQuery(id+"F3.wireOp",EDGE,"2c81646e-4cb3-4f6a-b688-8c6a1ed544cc.8.1");Q36=makeQuery(id+"F3.imprint","IMPRINT",FACE,{"disambiguationData":[TD([[makeQuery(id+"F3.imprint","IMPRINT",EDGE,{"derivedFrom":subQ1}),-1.0]])]});}
            var Q37;
            {var subQ1=sQuery(id+"F3.wireOp",EDGE,"2c81646e-4cb3-4f6a-b688-8c6a1ed544cc.7.1");Q37=makeQuery(id+"F3.imprint","IMPRINT",FACE,{"disambiguationData":[TD([[makeQuery(id+"F3.imprint","IMPRINT",EDGE,{"derivedFrom":subQ1}),-1.0]])]});}
            var Q38;
            {var subQ138=sQuery(id+"F3.wireOp",EDGE,"E31");Q38=makeQuery(id+"F3.imprint","IMPRINT",FACE,{"disambiguationData":[TD([[makeQuery(id+"F3.imprint","IMPRINT",EDGE,{"derivedFrom":subQ138}),1.0]])]});}
            var Q39;
            {var subQ6=sQuery(id+"F3.wireOp",EDGE,"E39.1.6.0");Q39=makeQuery(id+"F3.imprint","IMPRINT",FACE,{"disambiguationData":[TD([[makeQuery(id+"F3.imprint","IMPRINT",EDGE,{"derivedFrom":subQ6}),-1.0]])]});}
            var Q40;
            {var subQ6=sQuery(id+"F3.wireOp",EDGE,"E39.1.5.0");Q40=makeQuery(id+"F3.imprint","IMPRINT",FACE,{"disambiguationData":[TD([[makeQuery(id+"F3.imprint","IMPRINT",EDGE,{"derivedFrom":subQ6}),-1.0]])]});}
            var Q41;
            {var subQ6=sQuery(id+"F3.wireOp",EDGE,"E39.1.4.0");Q41=makeQuery(id+"F3.imprint","IMPRINT",FACE,{"disambiguationData":[TD([[makeQuery(id+"F3.imprint","IMPRINT",EDGE,{"derivedFrom":subQ6}),-1.0]])]});}
            var Q42;
            {var subQ6=sQuery(id+"F3.wireOp",EDGE,"E39.1.3.0");Q42=makeQuery(id+"F3.imprint","IMPRINT",FACE,{"disambiguationData":[TD([[makeQuery(id+"F3.imprint","IMPRINT",EDGE,{"derivedFrom":subQ6}),-1.0]])]});}
            var Q43;
            {var subQ6=sQuery(id+"F3.wireOp",EDGE,"E38.2.0");Q43=makeQuery(id+"F3.imprint","IMPRINT",FACE,{"disambiguationData":[TD([[makeQuery(id+"F3.imprint","IMPRINT",EDGE,{"derivedFrom":subQ6}),-1.0]])]});}
            var Q44;
            {var subQ6=sQuery(id+"F3.wireOp",EDGE,"E38.1.0");Q44=makeQuery(id+"F3.imprint","IMPRINT",FACE,{"disambiguationData":[TD([[makeQuery(id+"F3.imprint","IMPRINT",EDGE,{"derivedFrom":subQ6}),-1.0]])]});}
            var Q45;
            {var subQ5=sQuery(id+"F3.wireOp",EDGE,"E36");Q45=makeQuery(id+"F3.imprint","IMPRINT",FACE,{"disambiguationData":[TD([[makeQuery(id+"F3.imprint","IMPRINT",EDGE,{"derivedFrom":subQ5}),-1.0]])]});}
            var Q46;
            {var subQ5=sQuery(id+"F3.wireOp",EDGE,"E37.MirrorCS");Q46=makeQuery(id+"F3.imprint","IMPRINT",FACE,{"disambiguationData":[TD([[makeQuery(id+"F3.imprint","IMPRINT",EDGE,{"derivedFrom":subQ5}),1.0]])]});}
            var Q47;
            {var subQ6=sQuery(id+"F3.wireOp",EDGE,"E39.1.34.0");Q47=makeQuery(id+"F3.imprint","IMPRINT",FACE,{"disambiguationData":[TD([[makeQuery(id+"F3.imprint","IMPRINT",EDGE,{"derivedFrom":subQ6}),-1.0]])]});}
            var Q48;
            {var subQ6=sQuery(id+"F3.wireOp",EDGE,"E39.1.33.0");Q48=makeQuery(id+"F3.imprint","IMPRINT",FACE,{"disambiguationData":[TD([[makeQuery(id+"F3.imprint","IMPRINT",EDGE,{"derivedFrom":subQ6}),-1.0]])]});}
            var Q49;
            {var subQ6=sQuery(id+"F3.wireOp",EDGE,"E39.1.32.0");Q49=makeQuery(id+"F3.imprint","IMPRINT",FACE,{"disambiguationData":[TD([[makeQuery(id+"F3.imprint","IMPRINT",EDGE,{"derivedFrom":subQ6}),-1.0]])]});}
            var Q50;
            {var subQ6=sQuery(id+"F3.wireOp",EDGE,"E39.1.31.0");Q50=makeQuery(id+"F3.imprint","IMPRINT",FACE,{"disambiguationData":[TD([[makeQuery(id+"F3.imprint","IMPRINT",EDGE,{"derivedFrom":subQ6}),-1.0]])]});}
            var Q51;
            {var subQ6=sQuery(id+"F3.wireOp",EDGE,"E39.1.30.0");Q51=makeQuery(id+"F3.imprint","IMPRINT",FACE,{"disambiguationData":[TD([[makeQuery(id+"F3.imprint","IMPRINT",EDGE,{"derivedFrom":subQ6}),-1.0]])]});}
            var Q52;
            {var subQ7=sQuery(id+"F3.wireOp",EDGE,"E39.1.29.0");Q52=makeQuery(id+"F3.imprint","IMPRINT",FACE,{"disambiguationData":[TD([[makeQuery(id+"F3.imprint","IMPRINT",EDGE,{"derivedFrom":subQ7}),-1.0]])]});}
            var Q53;
            {var subQ6=sQuery(id+"F3.wireOp",EDGE,"E39.1.28.0");Q53=makeQuery(id+"F3.imprint","IMPRINT",FACE,{"disambiguationData":[TD([[makeQuery(id+"F3.imprint","IMPRINT",EDGE,{"derivedFrom":subQ6}),-1.0]])]});}
            var Q54;
            {var subQ6=sQuery(id+"F3.wireOp",EDGE,"E39.1.27.0");Q54=makeQuery(id+"F3.imprint","IMPRINT",FACE,{"disambiguationData":[TD([[makeQuery(id+"F3.imprint","IMPRINT",EDGE,{"derivedFrom":subQ6}),-1.0]])]});}
            var Q55;
            {var subQ6=sQuery(id+"F3.wireOp",EDGE,"E39.1.26.0");Q55=makeQuery(id+"F3.imprint","IMPRINT",FACE,{"disambiguationData":[TD([[makeQuery(id+"F3.imprint","IMPRINT",EDGE,{"derivedFrom":subQ6}),-1.0]])]});}
            var Q56;
            {var subQ6=sQuery(id+"F3.wireOp",EDGE,"E39.1.25.0");Q56=makeQuery(id+"F3.imprint","IMPRINT",FACE,{"disambiguationData":[TD([[makeQuery(id+"F3.imprint","IMPRINT",EDGE,{"derivedFrom":subQ6}),-1.0]])]});}
            var Q57;
            {var subQ6=sQuery(id+"F3.wireOp",EDGE,"E39.1.24.0");Q57=makeQuery(id+"F3.imprint","IMPRINT",FACE,{"disambiguationData":[TD([[makeQuery(id+"F3.imprint","IMPRINT",EDGE,{"derivedFrom":subQ6}),-1.0]])]});}
            var Q58;
            {var subQ6=sQuery(id+"F3.wireOp",EDGE,"E39.1.23.0");Q58=makeQuery(id+"F3.imprint","IMPRINT",FACE,{"disambiguationData":[TD([[makeQuery(id+"F3.imprint","IMPRINT",EDGE,{"derivedFrom":subQ6}),-1.0]])]});}
            var Q59;
            {var subQ6=sQuery(id+"F3.wireOp",EDGE,"E39.1.22.0");Q59=makeQuery(id+"F3.imprint","IMPRINT",FACE,{"disambiguationData":[TD([[makeQuery(id+"F3.imprint","IMPRINT",EDGE,{"derivedFrom":subQ6}),-1.0]])]});}
            var Q60;
            {var subQ6=sQuery(id+"F3.wireOp",EDGE,"E39.1.21.0");Q60=makeQuery(id+"F3.imprint","IMPRINT",FACE,{"disambiguationData":[TD([[makeQuery(id+"F3.imprint","IMPRINT",EDGE,{"derivedFrom":subQ6}),-1.0]])]});}
            var Q61;
            {var subQ6=sQuery(id+"F3.wireOp",EDGE,"E39.1.20.0");Q61=makeQuery(id+"F3.imprint","IMPRINT",FACE,{"disambiguationData":[TD([[makeQuery(id+"F3.imprint","IMPRINT",EDGE,{"derivedFrom":subQ6}),-1.0]])]});}
            var Q62;
            {var subQ6=sQuery(id+"F3.wireOp",EDGE,"E39.1.19.0");Q62=makeQuery(id+"F3.imprint","IMPRINT",FACE,{"disambiguationData":[TD([[makeQuery(id+"F3.imprint","IMPRINT",EDGE,{"derivedFrom":subQ6}),-1.0]])]});}
            var Q63;
            {var subQ7=sQuery(id+"F3.wireOp",EDGE,"E39.1.18.0");Q63=makeQuery(id+"F3.imprint","IMPRINT",FACE,{"disambiguationData":[TD([[makeQuery(id+"F3.imprint","IMPRINT",EDGE,{"derivedFrom":subQ7}),-1.0]])]});}
            var Q64;
            {var subQ6=sQuery(id+"F3.wireOp",EDGE,"E39.1.17.0");Q64=makeQuery(id+"F3.imprint","IMPRINT",FACE,{"disambiguationData":[TD([[makeQuery(id+"F3.imprint","IMPRINT",EDGE,{"derivedFrom":subQ6}),-1.0]])]});}
            var Q65;
            {var subQ6=sQuery(id+"F3.wireOp",EDGE,"E39.1.16.0");Q65=makeQuery(id+"F3.imprint","IMPRINT",FACE,{"disambiguationData":[TD([[makeQuery(id+"F3.imprint","IMPRINT",EDGE,{"derivedFrom":subQ6}),-1.0]])]});}
            var Q66;
            {var subQ6=sQuery(id+"F3.wireOp",EDGE,"E39.1.15.0");Q66=makeQuery(id+"F3.imprint","IMPRINT",FACE,{"disambiguationData":[TD([[makeQuery(id+"F3.imprint","IMPRINT",EDGE,{"derivedFrom":subQ6}),-1.0]])]});}
            var Q67;
            {var subQ6=sQuery(id+"F3.wireOp",EDGE,"E39.1.14.0");Q67=makeQuery(id+"F3.imprint","IMPRINT",FACE,{"disambiguationData":[TD([[makeQuery(id+"F3.imprint","IMPRINT",EDGE,{"derivedFrom":subQ6}),-1.0]])]});}
            var Q68;
            {var subQ6=sQuery(id+"F3.wireOp",EDGE,"E39.1.13.0");Q68=makeQuery(id+"F3.imprint","IMPRINT",FACE,{"disambiguationData":[TD([[makeQuery(id+"F3.imprint","IMPRINT",EDGE,{"derivedFrom":subQ6}),-1.0]])]});}
            var Q69;
            {var subQ6=sQuery(id+"F3.wireOp",EDGE,"E39.1.12.0");Q69=makeQuery(id+"F3.imprint","IMPRINT",FACE,{"disambiguationData":[TD([[makeQuery(id+"F3.imprint","IMPRINT",EDGE,{"derivedFrom":subQ6}),-1.0]])]});}
            var Q70;
            {var subQ6=sQuery(id+"F3.wireOp",EDGE,"E39.1.11.0");Q70=makeQuery(id+"F3.imprint","IMPRINT",FACE,{"disambiguationData":[TD([[makeQuery(id+"F3.imprint","IMPRINT",EDGE,{"derivedFrom":subQ6}),-1.0]])]});}
            var Q71;
            {var subQ6=sQuery(id+"F3.wireOp",EDGE,"E39.1.10.0");Q71=makeQuery(id+"F3.imprint","IMPRINT",FACE,{"disambiguationData":[TD([[makeQuery(id+"F3.imprint","IMPRINT",EDGE,{"derivedFrom":subQ6}),-1.0]])]});}
            var Q72;
            {var subQ6=sQuery(id+"F3.wireOp",EDGE,"E39.1.9.0");Q72=makeQuery(id+"F3.imprint","IMPRINT",FACE,{"disambiguationData":[TD([[makeQuery(id+"F3.imprint","IMPRINT",EDGE,{"derivedFrom":subQ6}),-1.0]])]});}
            var Q73;
            {var subQ6=sQuery(id+"F3.wireOp",EDGE,"E39.1.8.0");Q73=makeQuery(id+"F3.imprint","IMPRINT",FACE,{"disambiguationData":[TD([[makeQuery(id+"F3.imprint","IMPRINT",EDGE,{"derivedFrom":subQ6}),-1.0]])]});}
            var Q74;
            {var subQ7=sQuery(id+"F3.wireOp",EDGE,"E39.1.7.0");Q74=makeQuery(id+"F3.imprint","IMPRINT",FACE,{"disambiguationData":[TD([[makeQuery(id+"F3.imprint","IMPRINT",EDGE,{"derivedFrom":subQ7}),-1.0]])]});}
            extrude(context, id + "F4", {"entities" : qUnion([Q0, Q1, Q2, Q3, Q4, Q5, Q6, Q7, Q8, Q9, Q10, Q11, Q12, Q13, Q14, Q15, Q16, Q17, Q18, Q19, Q20, Q21, Q22, Q23, Q24, Q25, Q26, Q27, Q28, Q29, Q30, Q31, Q32, Q33, Q34, Q35, Q36, Q37, Q38, Q39, Q40, Q41, Q42, Q43, Q44, Q45, Q46, Q47, Q48, Q49, Q50, Q51, Q52, Q53, Q54, Q55, Q56, Q57, Q58, Q59, Q60, Q61, Q62, Q63, Q64, Q65, Q66, Q67, Q68, Q69, Q70, Q71, Q72, Q73, Q74]), "operationType" : NewBodyOperationType.INTERSECT, "oppositeDirection" : true, "depth" : 13.3 * mm});
        }
        {
            var Q0;
            Q0=makeQuery(id+"F1.opRevolve","SWEPT_FACE",FACE,{"disambiguationData":[OSD([sQuery(id+"F0.wireOp",EDGE,"E6.MirrorCS")])]});
            var sketch = newSketch(context, id + "F5", { "sketchPlane" : qUnion([Q0])});
            skLineSegment(sketch, "E40", {"start": v(0, 0) * mm, "end": v(-2.5, 0) * mm, "construction": true});
            skLineSegment(sketch, "E41", {"start": v(-2.5, 0) * mm, "end": v(-2.5, -1) * mm});
            skLineSegment(sketch, "E42", {"start": v(0, 0) * mm, "end": v(0, -2.5) * mm, "construction": true});
            skLineSegment(sketch, "E43", {"start": v(0, -2.5) * mm, "end": v(-1, -2.5) * mm});
            skLineSegment(sketch, "E44", {"start": v(-1, -2.5) * mm, "end": v(-1, -1) * mm});
            skLineSegment(sketch, "E45", {"start": v(-1, -1) * mm, "end": v(-2.5, -1) * mm});
            skLineSegment(sketch, "E46.MirrorCS", {"start": v(0, -2.5) * mm, "end": v(1, -2.5) * mm});
            skLineSegment(sketch, "E47.MirrorCS", {"start": v(1, -2.5) * mm, "end": v(1, -1) * mm});
            skLineSegment(sketch, "E48.MirrorCS", {"start": v(1, -1) * mm, "end": v(2.5, -1) * mm});
            skLineSegment(sketch, "E49.MirrorCS", {"start": v(2.5, 0) * mm, "end": v(2.5, -1) * mm});
            skLineSegment(sketch, "E50.MirrorCS", {"start": v(-2.5, 0) * mm, "end": v(-2.5, 1) * mm});
            skLineSegment(sketch, "E51.MirrorCS", {"start": v(-1, 1) * mm, "end": v(-2.5, 1) * mm});
            skLineSegment(sketch, "E52.MirrorCS", {"start": v(-1, 2.5) * mm, "end": v(-1, 1) * mm});
            skLineSegment(sketch, "E53.MirrorCS", {"start": v(0, 2.5) * mm, "end": v(-1, 2.5) * mm});
            skLineSegment(sketch, "E54.MirrorCS", {"start": v(0, 2.5) * mm, "end": v(1, 2.5) * mm});
            skLineSegment(sketch, "E55.MirrorCS", {"start": v(1, 2.5) * mm, "end": v(1, 1) * mm});
            skLineSegment(sketch, "E56.MirrorCS", {"start": v(1, 1) * mm, "end": v(2.5, 1) * mm});
            skLineSegment(sketch, "E57.MirrorCS", {"start": v(2.5, 0) * mm, "end": v(2.5, 1) * mm});
            skSolve(sketch);
        }
        {
            var Q0;
            Q0=makeQuery(id+"F5.imprint","IMPRINT",FACE,{"disambiguationData":[TD([[makeQuery(id+"F5.imprint","IMPRINT",EDGE,{"derivedFrom":sQuery(id+"F5.wireOp",EDGE,"E41")}),1.0]])]});
            extrude(context, id + "F6", {"entities" : qUnion([Q0]), "operationType" : NewBodyOperationType.REMOVE, "oppositeDirection" : true, "depth" : 25 * mm});
        }
    });
